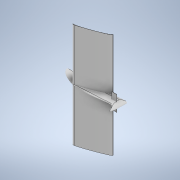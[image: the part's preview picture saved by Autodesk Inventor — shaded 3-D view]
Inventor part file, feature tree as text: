
AUTODESK INVENTOR PART (.ipt)
format: ipt  version: 2022 (Build 260153000, 153)  size: 498,176 bytes
history: native  units: mm
features: other x3, extrude x2, sketch x2, fillet x1
ambient origin geometry x8: Origin, YZ Plane, XZ Plane, XY Plane, X Axis, Y Axis, Z Axis, Center Point
bodies: Body1 (feature_tree), Body2 (feature_tree)
feature tree (8):
  other  "ソリッド1"
  extrude  "押し出し1"  Depth=1.047198mm TaperAngle=0.0deg
  extrude  "押し出し2"  Depth=2.0mm
  fillet  "フィレット6"  Radius=50.0mm
  other  "フォーム2"
  sketch  "スケッチ1"
  sketch  "スケッチ3"
  other  "ソリッド2"
